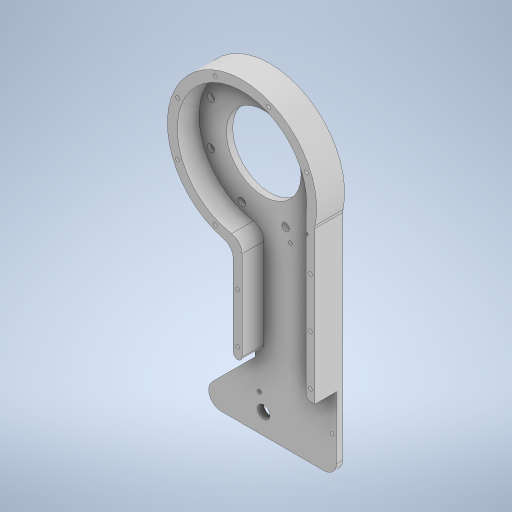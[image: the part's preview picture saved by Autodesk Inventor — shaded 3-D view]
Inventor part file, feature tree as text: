
AUTODESK INVENTOR PART (.ipt)
format: ipt  version: 2024.3 (Build 283343000, 343)  size: 480,256 bytes
history: native  units: mm
features: sketch x11, extrude x6, hole x5, fillet x3, other x1
ambient origin geometry x8: Origin, YZ Plane, XZ Plane, XY Plane, X Axis, Y Axis, Z Axis, Center Point
bodies: Body1 (feature_tree)
feature tree (26):
  other  "ソリッド1"
  extrude  "押し出し1"  Depth=120.0mm
  hole  "穴1"  [1 undecoded]
  extrude  "押し出し3"  Depth=5.0mm TaperAngle=0.0deg
  hole  "穴6"  [1 undecoded]
  hole  "穴7"  [1 undecoded]
  extrude  "押し出し10"  Depth=80.0mm TaperAngle=360.0deg
  extrude  "押し出し11"  Depth=58.5mm
  extrude  "押し出し12"  Depth=117.0mm
  hole  "穴8"  [1 undecoded]
  fillet  "フィレット4"  Radius=210.0mm
  fillet  "フィレット5"  Radius=5.0mm
  fillet  "フィレット6"  [1 undecoded]
  extrude  "押し出し13"  Depth=14.835299mm
  hole  "穴9"  [1 undecoded]
  sketch  "スケッチ1"
  sketch  "スケッチ2"
  sketch  "スケッチ4"
  sketch  "スケッチ15"
  sketch  "スケッチ16"
  sketch  "スケッチ17"
  sketch  "スケッチ18"
  sketch  "スケッチ19"
  sketch  "スケッチ20"
  sketch  "スケッチ21"
  sketch  "スケッチ22"
note: 6 required parameter values undecoded (feature->parameter linkage not recoverable at this tier; creation-order binding heuristic only, values carry confidence <= 0.55)
